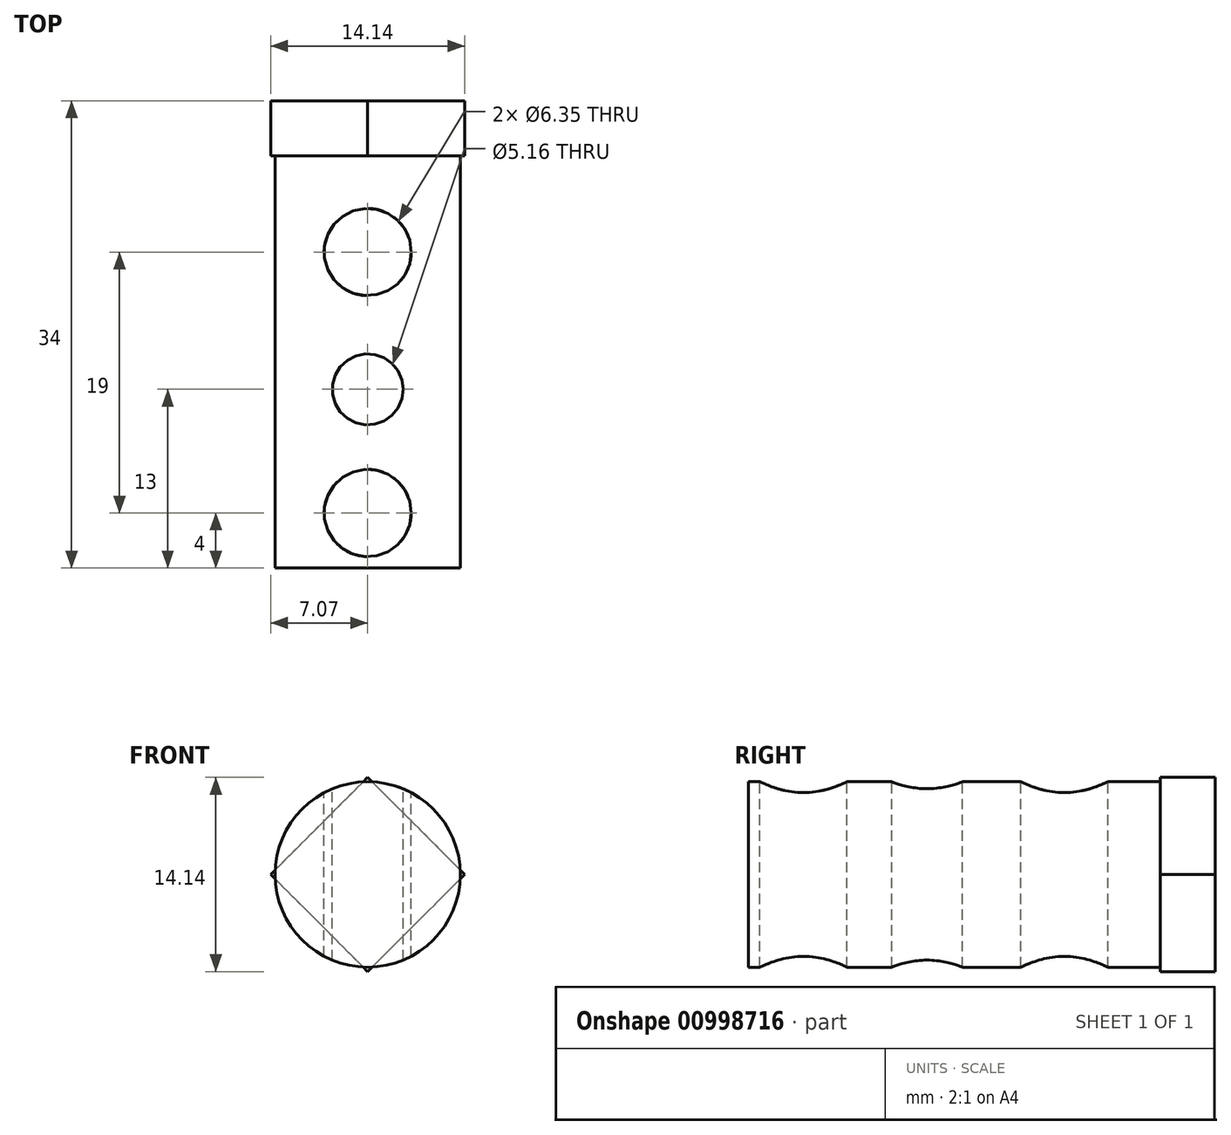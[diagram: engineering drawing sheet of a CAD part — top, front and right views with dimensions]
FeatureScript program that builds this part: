
annotation { "Feature Type Name" : "Feature", "Feature Type Description" : "" }
export const myFeature = defineFeature(function(context is Context, id is Id, definition is map)
    precondition{}
    {
        {
            var Q0;
            Q0=qCreatedBy(makeId("Front.planeOp"),FACE);
            var sketch = newSketch(context, id + "F0", { "sketchPlane" : qUnion([Q0])});
            skCircle(sketch, "E0", {"center": v(0, 0) * mm, "radius": 6.75 * mm});
            skSolve(sketch);
        }
        {
            var Q0;
            Q0 = qSketchRegion(id + "F0", true);
            extrude(context, id + "F1", {"entities" : qUnion([Q0]), "oppositeDirection" : true, "depth" : 13 * mm, "offsetDistance" : 25 * mm, "hasSecondDirection" : true, "secondDirectionOppositeDirection" : false, "secondDirectionDepth" : 17 * mm});
        }
        {
            var Q0;
            Q0=qCreatedBy(makeId("Top.planeOp"),FACE);
            var sketch = newSketch(context, id + "F2", { "sketchPlane" : qUnion([Q0])});
            skLineSegment(sketch, "E1", {"start": v(0, -53.15) * mm, "end": v(0, 53.15) * mm, "construction": true});
            skCircle(sketch, "E2", {"center": v(0, 6) * mm, "radius": 3.18 * mm});
            skCircle(sketch, "E3", {"center": v(0, -4) * mm, "radius": 2.58 * mm});
            skCircle(sketch, "E4", {"center": v(0, -13) * mm, "radius": 3.18 * mm});
            skLineSegment(sketch, "E5.1.0", {"start": v(-6.75, 13) * mm, "end": v(6.75, 13) * mm, "construction": true});
            skSolve(sketch);
        }
        {
            var Q0;
            Q0 = qSketchRegion(id + "F2", true);
            extrude(context, id + "F3", {"entities" : qUnion([Q0]), "operationType" : NewBodyOperationType.REMOVE, "endBound" : BoundingType.THROUGH_ALL, "oppositeDirection" : true, "depth" : 25 * mm, "offsetDistance" : 25 * mm, "hasSecondDirection" : true, "secondDirectionBound" : SecondDirectionBoundingType.THROUGH_ALL, "secondDirectionOppositeDirection" : false, "secondDirectionDepth" : 25 * mm});
        }
        {
            var Q0;
            Q0=makeQuery(id+"F1.opExtrude","CAP_FACE",FACE,{"disambiguationData":[OSD([sQuery(id+"F0.wireOp",EDGE,"E0")])],"isStart":false});
            var sketch = newSketch(context, id + "F4", { "sketchPlane" : qUnion([Q0])});
            skCircle(sketch, "E6.cCircle", {"center": v(0, 0) * mm, "radius": 5 * mm, "construction": true});
            skLineSegment(sketch, "E6.0", {"start": v(0, -7.07) * mm, "end": v(-7.07, 0) * mm});
            skLineSegment(sketch, "E6.1", {"start": v(-7.07, 0) * mm, "end": v(0, 7.07) * mm});
            skLineSegment(sketch, "E6.2", {"start": v(0, 7.07) * mm, "end": v(7.07, 0) * mm});
            skLineSegment(sketch, "E6.3", {"start": v(7.07, 0) * mm, "end": v(0, -7.07) * mm});
            skPoint(sketch, "E6.0.midPoint", {"position": v(-3.54, -3.54) * mm});
            skLineSegment(sketch, "E7", {"start": v(0, 0) * mm, "end": v(-7.07, 0) * mm, "construction": true});
            skSolve(sketch);
        }
        {
            var Q0;
            Q0 = qSketchRegion(id + "F4", true);
            extrude(context, id + "F5", {"entities" : qUnion([Q0]), "operationType" : NewBodyOperationType.ADD, "depth" : 4 * mm, "offsetDistance" : 25 * mm});
        }
    });
